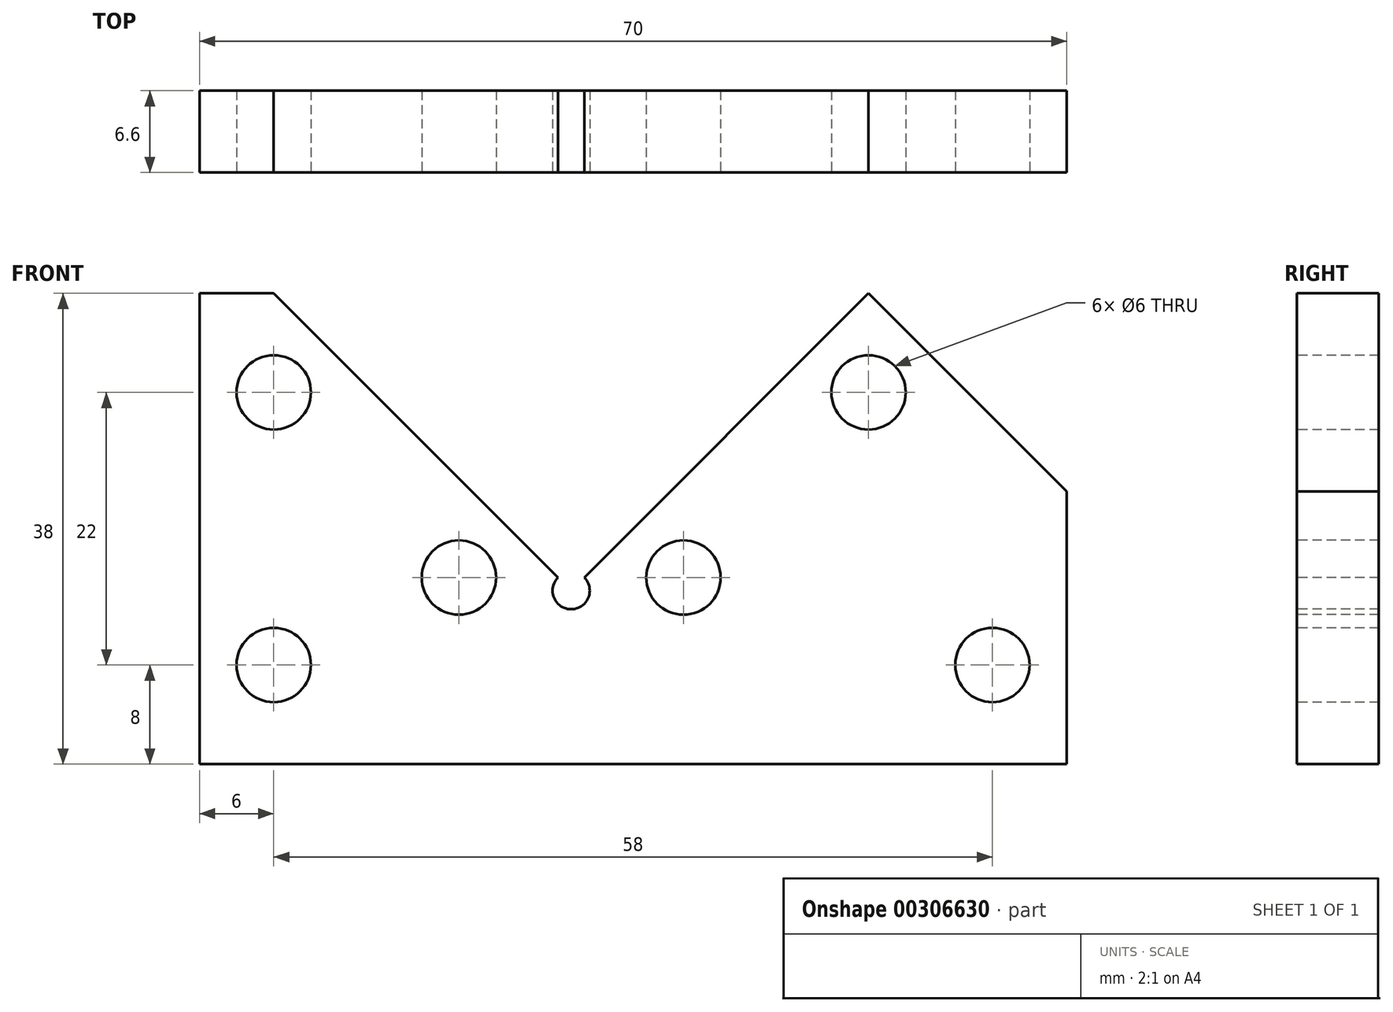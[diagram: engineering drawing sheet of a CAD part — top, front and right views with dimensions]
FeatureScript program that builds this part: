
annotation { "Feature Type Name" : "Feature", "Feature Type Description" : "" }
export const myFeature = defineFeature(function(context is Context, id is Id, definition is map)
    precondition{}
    {
        {
            var Q0;
            Q0=qCreatedBy(makeId("Front.planeOp"),FACE);
            var sketch = newSketch(context, id + "F0", { "sketchPlane" : qUnion([Q0])});
            skLineSegment(sketch, "E0", {"start": v(0, 0) * mm, "end": v(0, 38) * mm});
            skLineSegment(sketch, "E1", {"start": v(0, 38) * mm, "end": v(6, 38) * mm});
            skLineSegment(sketch, "E2", {"start": v(6, 38) * mm, "end": v(28.94, 15.06) * mm});
            skLineSegment(sketch, "E3", {"start": v(31.06, 15.06) * mm, "end": v(54, 38) * mm});
            skLineSegment(sketch, "E4", {"start": v(54, 38) * mm, "end": v(70, 22) * mm});
            skLineSegment(sketch, "E5", {"start": v(70, 22) * mm, "end": v(70, 0) * mm});
            skLineSegment(sketch, "E6", {"start": v(70, 0) * mm, "end": v(0, 0) * mm});
            skArc(sketch, "E7", {"start": v(28.94, 15.06) * mm, "mid": v(30, 12.5) * mm, "end": v(31.06, 15.06) * mm});
            skCircle(sketch, "E8", {"center": v(6, 8) * mm, "radius": 3 * mm});
            skLineSegment(sketch, "E9", {"start": v(35, 0) * mm, "end": v(35, 10.07) * mm, "construction": true});
            skPoint(sketch, "E9.endSnap0", {"position": v(35, 0) * mm});
            skCircle(sketch, "E10.MirrorC", {"center": v(64, 8) * mm, "radius": 3 * mm});
            skCircle(sketch, "E11", {"center": v(6, 30) * mm, "radius": 3 * mm});
            skLineSegment(sketch, "E12", {"start": v(17.47, 26.53) * mm, "end": v(9.75, 18.81) * mm, "construction": true});
            skCircle(sketch, "E13.MirrorC", {"center": v(20.94, 15.06) * mm, "radius": 3 * mm});
            skLineSegment(sketch, "E14", {"start": v(30, 14) * mm, "end": v(30, 40.8) * mm, "construction": true});
            skCircle(sketch, "E15.MirrorC", {"center": v(54, 30) * mm, "radius": 3 * mm});
            skCircle(sketch, "E16.MirrorC", {"center": v(39.06, 15.06) * mm, "radius": 3 * mm});
            skSolve(sketch);
        }
        {
            var Q0;
            Q0=qSketchRegion(id+"F0",true);
            extrude(context, id + "F1", {"entities" : qUnion([Q0]), "oppositeDirection" : true, "depth" : 6.6 * mm});
        }
    });
